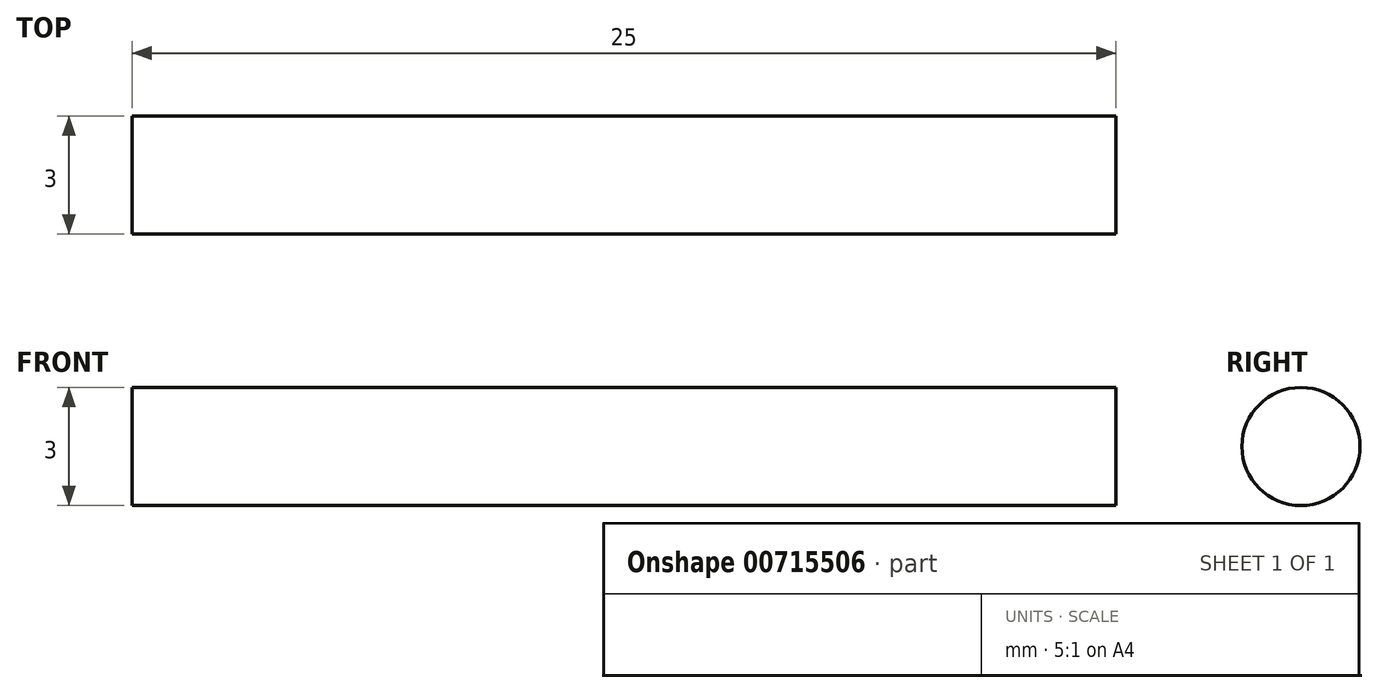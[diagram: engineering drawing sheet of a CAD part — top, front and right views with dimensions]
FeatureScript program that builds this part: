
annotation { "Feature Type Name" : "Feature", "Feature Type Description" : "" }
export const myFeature = defineFeature(function(context is Context, id is Id, definition is map)
    precondition{}
    {
        {
            var Q0;
            Q0=qCreatedBy(makeId("Right.planeOp"),FACE);
            var sketch = newSketch(context, id + "F0", { "sketchPlane" : qUnion([Q0])});
            skCircle(sketch, "E0", {"center": v(0, 0) * mm, "radius": 1.5 * mm});
            skSolve(sketch);
        }
        {
            var Q0;
            Q0 = qSketchRegion(id + "F0", true);
            extrude(context, id + "F1", {"entities" : qUnion([Q0]), "endBound" : BoundingType.SYMMETRIC, "oppositeDirection" : true, "depth" : 25 * mm, "offsetDistance" : 25 * mm});
        }
    });
